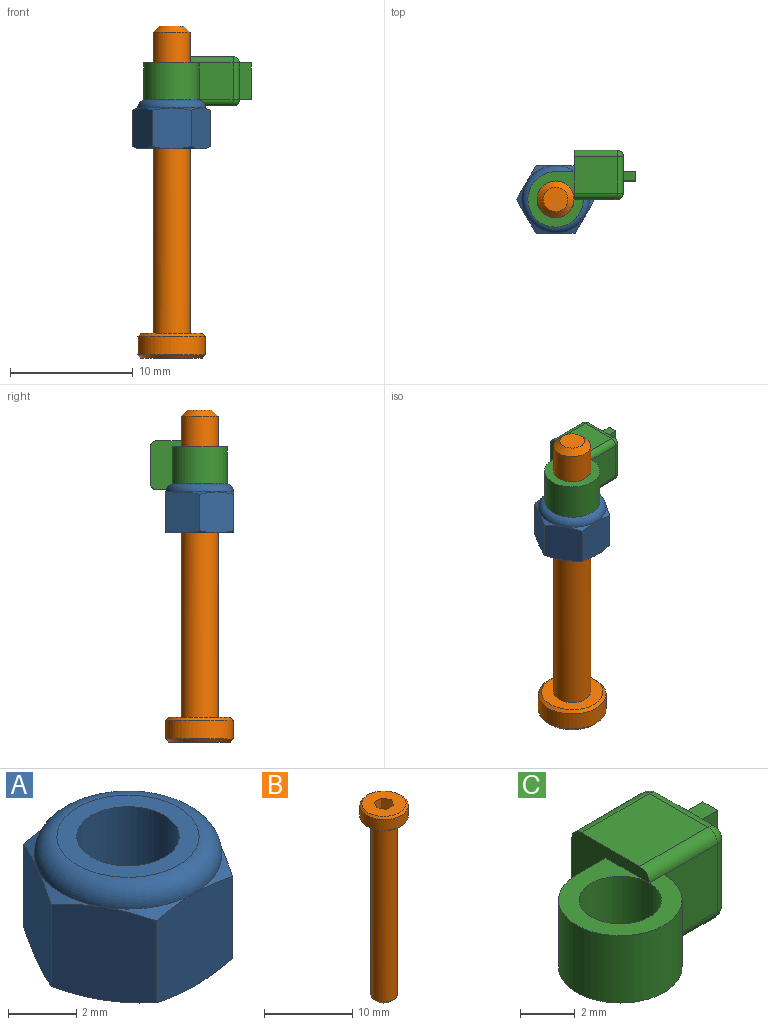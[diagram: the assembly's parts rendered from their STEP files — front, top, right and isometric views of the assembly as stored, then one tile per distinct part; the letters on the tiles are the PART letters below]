
ASSEMBLY  parts=3 mates=2
PART A: 22 faces, bbox 6.6x6.6x4.2 mm
  f0: plane 3.59x2.99mm, normal (-0.87,0.5,0), area 10.2mm2, adj f1,f5,f7,f9,f13,f14,f16,f21
  f1: plane 3.59x2.99mm, normal (-0.87,-0.5,0), area 10.2mm2, adj f0,f2,f7,f9,f10,f14,f20,f21
  f2: plane 3.6x3.42mm, normal (0,-1,0), area 10.2mm2, adj f1,f3,f7,f10,f11,f14,f19,f20
  f3: plane 3.59x2.99mm, normal (0.87,-0.5,0), area 10.2mm2, adj f2,f4,f7,f11,f12,f14,f18,f19
  f4: plane 3.59x2.99mm, normal (0.87,0.5,0), area 10.2mm2, adj f3,f5,f7,f12,f14,f15,f17,f18
  f5: plane 3.6x3.42mm, normal (0,1,0), area 10.2mm2, adj f0,f4,f7,f13,f14,f15,f16,f17
  f6: plane 4.17x4.17mm, normal (0,0,1), area 6.6mm2, adj f8,f14
  f7: plane 5.5x5.5mm, normal (0,0,-1), area 16.7mm2, adj f0,f1,f2,f3,f4,f5,f8,f16
  f8: cylinder r=1.5mm len=4mm, axis (0,0,1), area 37.7mm2, adj f6,f7
  f9: cone r=3.18mm half-angle=65deg, axis (0,0,-1), area 0.7mm2, adj f0,f1,f14
  f10: cone r=3.18mm half-angle=65deg, axis (0,0,-1), area 0.7mm2, adj f1,f2,f14
  f11: cone r=3.18mm half-angle=65deg, axis (0,0,-1), area 0.7mm2, adj f2,f3,f14
  f12: cone r=3.18mm half-angle=65deg, axis (0,0,-1), area 0.7mm2, adj f3,f4,f14
  f13: cone r=3.18mm half-angle=65deg, axis (0,0,-1), area 0.7mm2, adj f0,f5,f14
  f14: torus R=2.08mm, axis (0,0,-1), area 16.5mm2, adj f0,f1,f2,f3,f4,f5,f6,f9
  f15: cone r=3.18mm half-angle=65deg, axis (0,0,-1), area 0.7mm2, adj f4,f5,f14
  f16: cone r=2.75mm half-angle=65deg, axis (0,0,1), area 0.7mm2, adj f0,f5,f7
  f17: cone r=2.75mm half-angle=65deg, axis (0,0,1), area 0.7mm2, adj f4,f5,f7
  f18: cone r=2.75mm half-angle=65deg, axis (0,0,1), area 0.7mm2, adj f3,f4,f7
  f19: cone r=2.75mm half-angle=65deg, axis (0,0,1), area 0.7mm2, adj f2,f3,f7
  f20: cone r=2.75mm half-angle=65deg, axis (0,0,1), area 0.7mm2, adj f1,f2,f7
  f21: cone r=2.75mm half-angle=65deg, axis (0,0,1), area 0.7mm2, adj f0,f1,f7
PART B: 15 faces, bbox 5.5x5.5x27 mm
  f0: plane 5x5mm, normal (0,0,1), area 16.2mm2, adj f3,f4,f5,f6,f7,f8,f11
  f1: cylinder r=2.75mm len=5.5mm, axis (0,0,-1), area 25.9mm2, adj f10,f11
  f2: plane 5x5mm, normal (0,0,-1), area 12.6mm2, adj f10,f12
  f3: plane 1.5x1mm, normal (-0.87,-0.5,0), area 1.7mm2, adj f0,f4,f8,f9
  f4: plane 1.5x1.15mm, normal (0,-1,0), area 1.7mm2, adj f0,f3,f5,f9
  f5: plane 1.5x1mm, normal (0.87,-0.5,0), area 1.7mm2, adj f0,f4,f6,f9
  f6: plane 1.5x1mm, normal (0.87,0.5,0), area 1.7mm2, adj f0,f5,f7,f9
  f7: plane 1.5x1.15mm, normal (0,1,0), area 1.7mm2, adj f0,f6,f8,f9
  f8: plane 1.5x1mm, normal (-0.87,0.5,0), area 1.7mm2, adj f0,f3,f7,f9
  f9: plane 2.31x2mm, normal (0,0,1), area 3.5mm2, adj f3,f4,f5,f6,f7,f8
  f10: cone r=2.75mm half-angle=45deg, axis (0,0,1), area 5.8mm2, adj f1,f2
  f11: cone r=2.5mm half-angle=45deg, axis (0,0,-1), area 5.8mm2, adj f0,f1
  f12: cylinder r=1.5mm len=24.5mm, axis (0,0,1), area 230.9mm2, adj f2,f14
  f13: plane 2x2mm, normal (0,0,-1), area 3.1mm2, adj f14
  f14: cone r=1mm half-angle=45deg, axis (0,0,1), area 5.6mm2, adj f12,f13
PART C: 29 faces, bbox 8.8x6.3x4 mm
  f0: plane 3x1.25mm, normal (1,0,0), area 3.8mm2, adj f13,f18,f23,f24
  f1: cylinder r=2.25mm len=4.5mm, axis (0,0,-1), area 31.8mm2, adj f3,f4,f6,f16
  f2: cylinder r=1.5mm len=3mm, axis (0,0,-1), area 28.3mm2, adj f3,f4
  f3: plane 4.5x4.5mm, normal (0,0,1), area 8.2mm2, adj f1,f2,f5,f16,f22
  f4: plane 4.5x4.5mm, normal (0,0,-1), area 8.2mm2, adj f1,f2,f5,f16,f25
  f5: plane 4x4mm, normal (-1,0,0), area 9mm2, adj f3,f4,f8,f9,f10,f16,f17,f19
  f6: plane 3x2.75mm, normal (0,-1,0), area 8.2mm2, adj f1,f22,f25,f28
  f7: plane 3x1mm, normal (1,0,0), area 3mm2, adj f14,f23,f24,f28
  f8: plane 3.5x3mm, normal (0,1,0), area 10.5mm2, adj f5,f17,f18,f19
  f9: plane 3.5x3mm, normal (0,0,1), area 10.5mm2, adj f5,f17,f22,f23
  f10: plane 3.5x3mm, normal (0,0,-1), area 10.5mm2, adj f5,f19,f24,f25
  f11: plane 3x0.75mm, normal (1,0,0), area 2.2mm2, adj f12,f13,f14,f15
  f12: plane 1x0.75mm, normal (0,0,1), area 0.8mm2, adj f11,f13,f14,f23
  f13: plane 3x1mm, normal (0,1,0), area 3mm2, adj f0,f11,f12,f15
  f14: plane 3x1mm, normal (0,-1,0), area 3mm2, adj f7,f11,f12,f15
  f15: plane 1x0.75mm, normal (0,0,-1), area 0.8mm2, adj f11,f13,f14,f24
  f16: plane 3x1.5mm, normal (0,1,0), area 4.5mm2, adj f1,f3,f4,f5
  f17: cylinder r=0.5mm len=3.5mm, axis (1,0,0), area 2.7mm2, adj f5,f8,f9,f20
  f18: cylinder r=0.5mm len=3mm, axis (0,0,1), area 2.4mm2, adj f0,f8,f20,f21
  f19: cylinder r=0.5mm len=3.5mm, axis (-1,0,0), area 2.7mm2, adj f5,f8,f10,f21
  f20: sphere r=0.5mm, area 0.4mm2, adj f17,f18,f23
  f21: sphere r=0.5mm, area 0.4mm2, adj f18,f19,f24
  f22: cylinder r=0.5mm len=3.5mm, axis (-1,0,0), area 2.7mm2, adj f3,f5,f6,f9,f26
  f23: cylinder r=0.5mm len=3mm, axis (0,-1,0), area 2.4mm2, adj f0,f7,f9,f12,f20,f26
  f24: cylinder r=0.5mm len=3mm, axis (0,1,0), area 2.4mm2, adj f0,f7,f10,f15,f21,f27
  f25: cylinder r=0.5mm len=3.5mm, axis (1,0,0), area 2.7mm2, adj f4,f5,f6,f10,f27
  f26: sphere r=0.5mm, area 0.4mm2, adj f22,f23,f28
  f27: sphere r=0.5mm, area 0.4mm2, adj f24,f25,f28
  f28: cylinder r=0.5mm len=3mm, axis (0,0,-1), area 2.4mm2, adj f6,f7,f26,f27
PLACE A t=(-22.55,-24.82,1.81)mm
PLACE B rot(axis=(1,0,0),180deg) t=(27.45,-24.82,-13.19)mm
PLACE C t=(-22.55,-24.82,5.81)mm
MATE fastened C.f1 <-> A.f8  axis (0,0,-1) through (-22.55,-24.82,5.81)mm
MATE fastened B.f1 <-> A.f8  axis (0,0,1) through (-22.55,-24.82,-13.19)mm
